# Revit family: Haworth_Very_Chair_SideSeminarPerforated
name_source: partatom
category: Furniture
revit_build: Autodesk Revit 2018 (Build: 20170223_1515(x64)
units: mm (PartAtom-declared; Revit-internal decimal feet)

## family parameters
Always vertical = Yes
Cut with Voids When Loaded = No
OmniClass Number = 23.40.70.14.64.21
OmniClass Title = Systems Furniture
Room Calculation Point = No
Shared = No
Work Plane-Based = No

## types (3) — shared parameters
Actual Depth = 22"
Actual Height = 33 115/128"
Actual Width = 23 1/2"
Assembly Code = E2020200
Back Finish = Haworth _ Polymer _ Glacier
Casters = No
Chair Finish = Haworth _ Polymer _ Glacier
Cushion Finish = Haworth _ Fabric _ Tellure _ Sky 3A-32
Description = Perforated Side and Seminar
Frame Finish = Haworth _ Metal _ Chrome
Glide Finish = Haworth _ Polymer _ Slate
Manufacturer = Haworth
Model = Haworth - Chair - Very
Revision Number = 4
Size = Verify Final Dim. w/ Haworth
Sustainability Info = https://www.haworth.com
Tablet Bracket Finish = Haworth _ Paint _ Black
Tablet Edge Finish = Haworth _ Laminate _ Linen H-WL
Tablet Finish = Haworth _ Laminate _ Linen H-WL
URL = www.haworth.com
URL - Product = http://www.haworth.com
Warranty = http://www.haworth.com
With Back Cushion = No
With Seat Cushion = No

## per-type parameters (varying)
| type | Arms Actual | Tablet | With Arms |
| No Arms | No | No | No |
| Arms | Yes | No | Yes |
| Tablet | No | Yes | No |

## geometry (parser evidence)
native form markers: Blend x12, Sweep x6
no freeform markers — native parametric forms only
